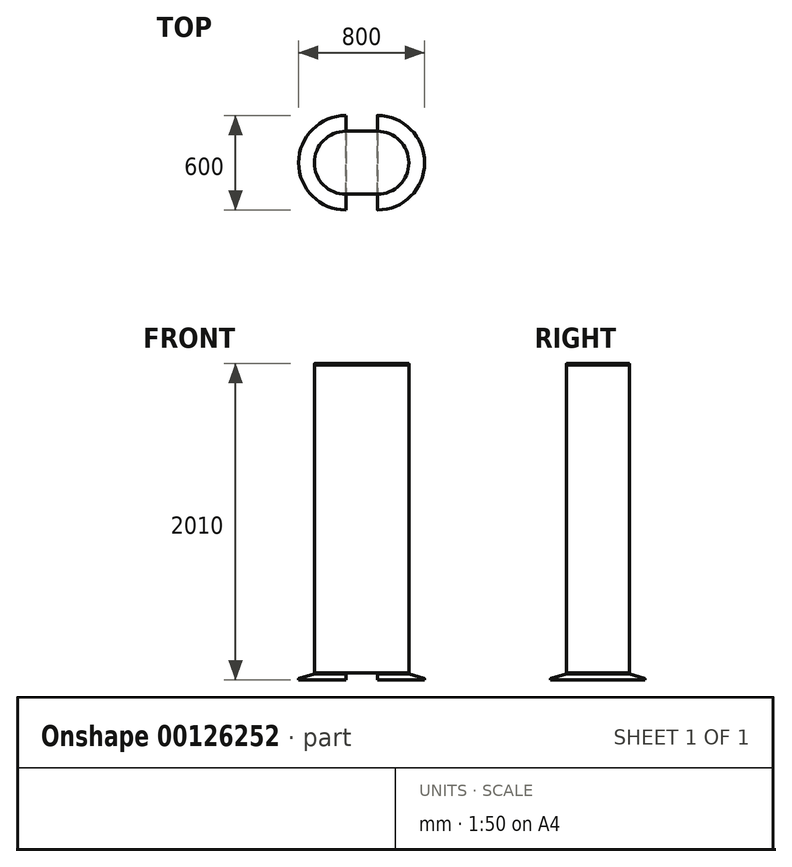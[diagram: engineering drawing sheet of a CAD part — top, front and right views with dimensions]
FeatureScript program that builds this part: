
annotation { "Feature Type Name" : "Feature", "Feature Type Description" : "" }
export const myFeature = defineFeature(function(context is Context, id is Id, definition is map)
    precondition{}
    {
        {
            var Q0;
            Q0=qCreatedBy(makeId("Right.planeOp"),FACE);
            var sketch = newSketch(context, id + "F0", { "sketchPlane" : qUnion([Q0])});
            skLineSegment(sketch, "E0", {"start": v(0, 0) * mm, "end": v(300, 0) * mm});
            skLineSegment(sketch, "E1", {"start": v(300, 0) * mm, "end": v(300, 10) * mm});
            skLineSegment(sketch, "E2", {"start": v(300, 10) * mm, "end": v(200, 10) * mm, "construction": true});
            skLineSegment(sketch, "E3", {"start": v(200, 10) * mm, "end": v(200, 40) * mm, "construction": true});
            skLineSegment(sketch, "E4", {"start": v(200, 40) * mm, "end": v(300, 10) * mm});
            skLineSegment(sketch, "E5", {"start": v(200, 40) * mm, "end": v(190, 40) * mm});
            skLineSegment(sketch, "E6", {"start": v(190, 40) * mm, "end": v(190, 45) * mm, "construction": true});
            skLineSegment(sketch, "E7", {"start": v(190, 45) * mm, "end": v(200, 45) * mm});
            skLineSegment(sketch, "E8", {"start": v(200, 45) * mm, "end": v(200, 2000) * mm});
            skLineSegment(sketch, "E9", {"start": v(0, 0) * mm, "end": v(0, 2000) * mm});
            skLineSegment(sketch, "E10", {"start": v(200, 2000) * mm, "end": v(0, 2000) * mm});
            skLineSegment(sketch, "E11", {"start": v(190, 40) * mm, "end": v(0, 40) * mm});
            skLineSegment(sketch, "E12", {"start": v(190, 45) * mm, "end": v(0, 45) * mm});
            skSolve(sketch);
        }
        {
            var Q0;
            Q0=makeQuery(id+"F0.imprint","IMPRINT",FACE,{"disambiguationData":[TD([[makeQuery(id+"F0.imprint","IMPRINT",EDGE,{"derivedFrom":sQuery(id+"F0.wireOp",EDGE,"E7")}),1.0]])]});
            var Q1;
            {var subQ0=sQuery(id+"F0.wireOp",EDGE,"E0");Q1=makeQuery(id+"F0.imprint","IMPRINT",FACE,{"disambiguationData":[TD([[makeQuery(id+"F0.imprint","IMPRINT",EDGE,{"derivedFrom":subQ0}),1.0]])]});}
            var Q2;
            Q2=sQuery(id+"F0.wireOp",EDGE,"E9");
            revolve(context, id + "F1", {"entities" : qUnion([Q0, Q1]), "axis" : qUnion([Q2]), "revolveType" : RevolveType.ONE_DIRECTION, "angle" : 180 * degree});
        }
        {
            var Q0;
            Q0=makeQuery(id+"F1.opRevolve","CAP_FACE",FACE,{"disambiguationData":[OSD([sQuery(id+"F0.wireOp",EDGE,"E7"),sQuery(id+"F0.wireOp",EDGE,"E8"),sQuery(id+"F0.wireOp",EDGE,"E9"),sQuery(id+"F0.wireOp",EDGE,"E10"),sQuery(id+"F0.wireOp",EDGE,"E12")])],"isStart":false});
            var Q1;
            Q1=makeQuery(id+"F1.opRevolve","CAP_FACE",FACE,{"disambiguationData":[OSD([sQuery(id+"F0.wireOp",EDGE,"E0"),sQuery(id+"F0.wireOp",EDGE,"E1"),sQuery(id+"F0.wireOp",EDGE,"E4"),sQuery(id+"F0.wireOp",EDGE,"E5"),sQuery(id+"F0.wireOp",EDGE,"E9"),sQuery(id+"F0.wireOp",EDGE,"E11")])],"isStart":true});
            extrude(context, id + "F2", {"entities" : qUnion([Q0, Q1]), "depth" : 200 * mm});
        }
        {
            var Q0;
            Q0=makeQuery(id+"F2.opExtrude","CAP_FACE",FACE,{"disambiguationData":[OSD([sQuery(id+"F0.wireOp",EDGE,"E7"),sQuery(id+"F0.wireOp",EDGE,"E8"),sQuery(id+"F0.wireOp",EDGE,"E9"),sQuery(id+"F0.wireOp",EDGE,"E10"),sQuery(id+"F0.wireOp",EDGE,"E12")])],"isStart":false});
            cPlane(context, id + "F3", {"entities" : qUnion([Q0]), "cplaneType" : CPlaneType.OFFSET, "offset" : 100 * mm, "oppositeDirection" : true, "width" : 150 * mm, "height" : 150 * mm});
        }
        {
            var Q0;
            Q0=makeQuery(id+"F1.opRevolve","SWEPT_BODY",BODY,{"disambiguationData":[OSD([sQuery(id+"F0.wireOp",EDGE,"E7"),sQuery(id+"F0.wireOp",EDGE,"E8"),sQuery(id+"F0.wireOp",EDGE,"E9"),sQuery(id+"F0.wireOp",EDGE,"E10"),sQuery(id+"F0.wireOp",EDGE,"E12")])]});
            var Q1;
            Q1=makeQuery(id+"F1.opRevolve","SWEPT_BODY",BODY,{"disambiguationData":[OSD([sQuery(id+"F0.wireOp",EDGE,"E0"),sQuery(id+"F0.wireOp",EDGE,"E1"),sQuery(id+"F0.wireOp",EDGE,"E4"),sQuery(id+"F0.wireOp",EDGE,"E5"),sQuery(id+"F0.wireOp",EDGE,"E9"),sQuery(id+"F0.wireOp",EDGE,"E11")])]});
            var Q2;
            Q2=qCreatedBy(id+"F3.planeOp",FACE);
            mirror(context, id + "F4", {"entities" : qUnion([Q0, Q1]), "mirrorPlane" : qUnion([Q2])});
        }
        {
            var Q0;
            Q0=makeQuery(id+"F4.opPattern","COPY",EDGE,{"derivedFrom":makeQuery(id+"F1.opRevolve","SWEPT_EDGE",EDGE,{"disambiguationData":[OSD([sQuery(id+"F0.wireOp",EDGE,"E1"),sQuery(id+"F0.wireOp",EDGE,"E4")])]}),"instanceName":"1"});
            var Q1;
            {var subQ0=sQuery(id+"F0.wireOp",EDGE,"E4");var subQ1=sQuery(id+"F0.wireOp",EDGE,"E1");Q1=makeQuery(id+"F2.opExtrude","SWEPT_EDGE",EDGE,{"disambiguationData":[OSD([subQ1,subQ0]),TDD([makeQuery(id+"F1.opRevolve","CAP_VERTEX",VERTEX,{"disambiguationData":[OSD([subQ1,subQ0])],"isStart":true})])]});}
            var Q2;
            Q2=makeQuery(id+"F1.opRevolve","SWEPT_EDGE",EDGE,{"disambiguationData":[OSD([sQuery(id+"F0.wireOp",EDGE,"E1"),sQuery(id+"F0.wireOp",EDGE,"E4")])]});
            var Q3;
            {var subQ0=sQuery(id+"F0.wireOp",EDGE,"E4");var subQ1=sQuery(id+"F0.wireOp",EDGE,"E1");Q3=makeQuery(id+"F2.opExtrude","SWEPT_EDGE",EDGE,{"disambiguationData":[OSD([subQ1,subQ0]),TDD([makeQuery(id+"F1.opRevolve","CAP_VERTEX",VERTEX,{"disambiguationData":[OSD([subQ1,subQ0])],"isStart":false})])]});}
            fillet(context, id + "F5", {"entities" : qUnion([Q0, Q1, Q2, Q3]), "radius" : 5 * mm, "tangentPropagation" : true, "allowEdgeOverflow" : false});
        }
        {
            var Q0;
            Q0=makeQuery(id+"F1.opRevolve","SWEPT_BODY",BODY,{"disambiguationData":[OSD([sQuery(id+"F0.wireOp",EDGE,"E7"),sQuery(id+"F0.wireOp",EDGE,"E8"),sQuery(id+"F0.wireOp",EDGE,"E9"),sQuery(id+"F0.wireOp",EDGE,"E10"),sQuery(id+"F0.wireOp",EDGE,"E12")])]});
            var Q1;
            Q1=makeQuery(id+"F2.opExtrude","SWEPT_BODY",BODY,{"disambiguationData":[OSD([sQuery(id+"F0.wireOp",EDGE,"E7"),sQuery(id+"F0.wireOp",EDGE,"E8"),sQuery(id+"F0.wireOp",EDGE,"E9"),sQuery(id+"F0.wireOp",EDGE,"E10"),sQuery(id+"F0.wireOp",EDGE,"E12")])]});
            var Q2;
            Q2=makeQuery(id+"F4.opPattern","COPY",BODY,{"derivedFrom":makeQuery(id+"F1.opRevolve","SWEPT_BODY",BODY,{"disambiguationData":[OSD([sQuery(id+"F0.wireOp",EDGE,"E7"),sQuery(id+"F0.wireOp",EDGE,"E8"),sQuery(id+"F0.wireOp",EDGE,"E9"),sQuery(id+"F0.wireOp",EDGE,"E10"),sQuery(id+"F0.wireOp",EDGE,"E12")])]}),"instanceName":"1"});
            booleanBodies(context, id + "F6", {"operationType" : BooleanOperationType.UNION, "tools" : qUnion([Q0, Q1, Q2])});
        }
        {
            var Q0;
            {var subQ0=sQuery(id+"F0.wireOp",EDGE,"E10");var subQ1=makeQuery(id+"F1.opRevolve","SWEPT_FACE",FACE,{"disambiguationData":[OSD([subQ0])]});Q0=makeQuery(id+"F6.opBoolean","MERGE",FACE,{"derivedFrom":[subQ1,makeQuery(id+"F2.opExtrude","SWEPT_FACE",FACE,{"disambiguationData":[OSD([subQ0])]}),makeQuery(id+"F4.opPattern","COPY",FACE,{"derivedFrom":subQ1,"instanceName":"1"})]});}
            extrude(context, id + "F7", {"entities" : qUnion([Q0]), "depth" : 10 * mm});
        }
        {
            var Q0;
            {var subQ0=sQuery(id+"F0.wireOp",EDGE,"E10");var subQ1=sQuery(id+"F0.wireOp",EDGE,"E8");Q0=makeQuery(id+"F7.opExtrude","CAP_EDGE",EDGE,{"disambiguationData":[OSD([subQ1,subQ0]),TDD([makeQuery(id+"F2.opExtrude","SWEPT_EDGE",EDGE,{"disambiguationData":[OSD([subQ1,subQ0]),TDD([makeQuery(id+"F1.opRevolve","CAP_VERTEX",VERTEX,{"disambiguationData":[OSD([subQ1,subQ0])],"isStart":false})])]})])],"isStart":false});}
            var Q1;
            {var subQ0=sQuery(id+"F0.wireOp",EDGE,"E10");var subQ1=sQuery(id+"F0.wireOp",EDGE,"E8");Q1=makeQuery(id+"F7.opExtrude","CAP_EDGE",EDGE,{"disambiguationData":[OSD([subQ1,subQ0]),TDD([makeQuery(id+"F1.opRevolve","SWEPT_EDGE",EDGE,{"disambiguationData":[OSD([subQ1,subQ0])]})])],"isStart":false});}
            fillet(context, id + "F8", {"entities" : qUnion([Q0, Q1]), "radius" : 2 * mm, "tangentPropagation" : true, "allowEdgeOverflow" : false});
        }
    });
